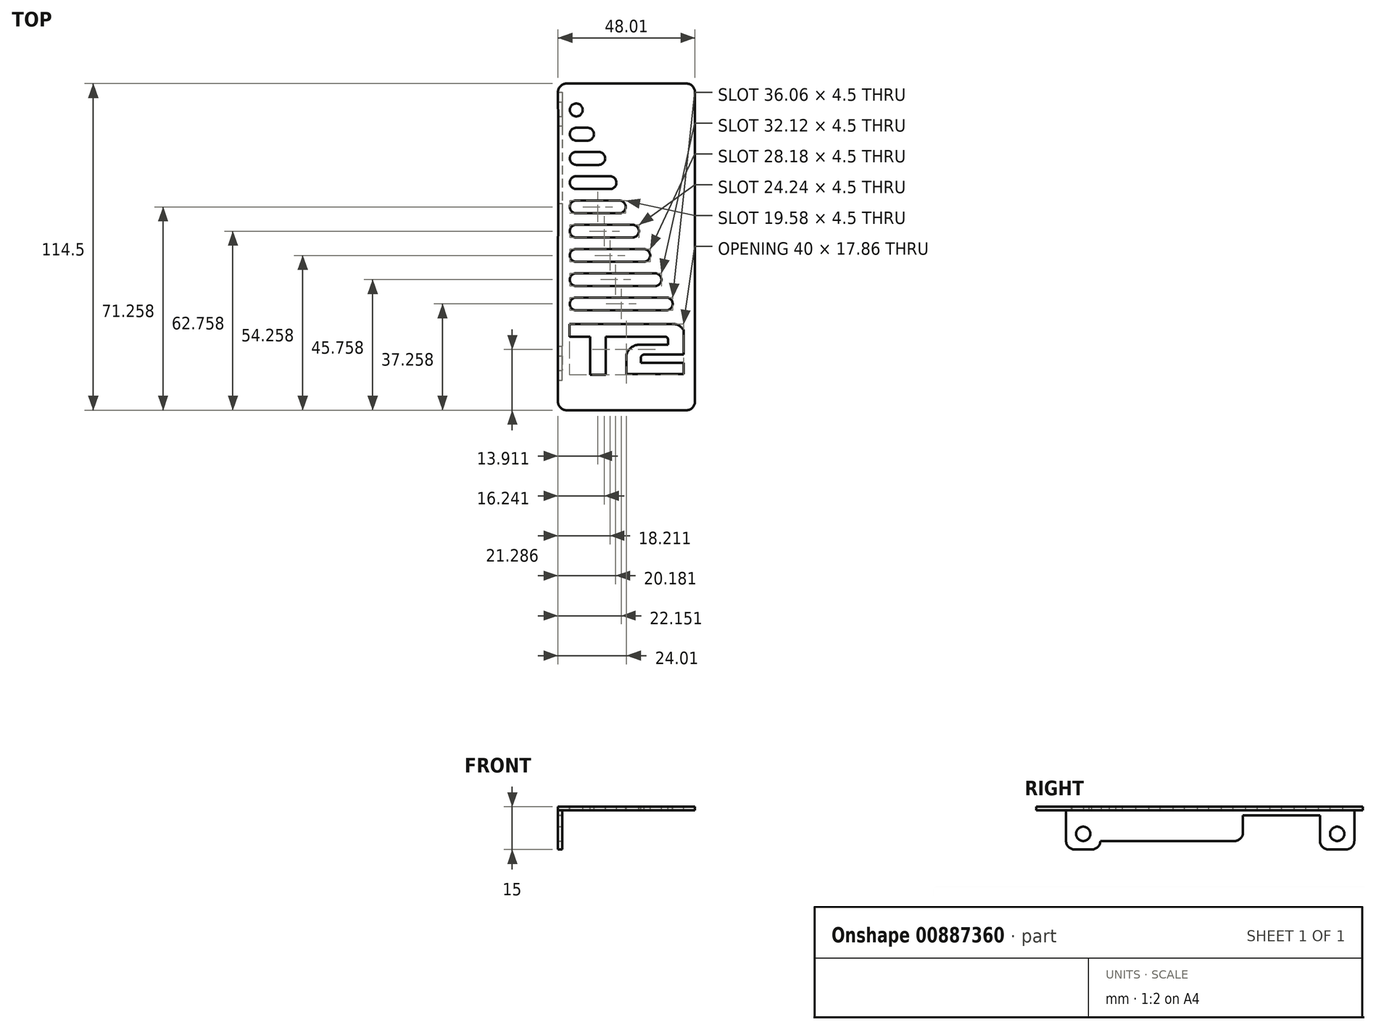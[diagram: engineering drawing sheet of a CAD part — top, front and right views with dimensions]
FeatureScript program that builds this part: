
annotation { "Feature Type Name" : "Feature", "Feature Type Description" : "" }
export const myFeature = defineFeature(function(context is Context, id is Id, definition is map)
    precondition{}
    {
        {
            var Q0;
            Q0=qCreatedBy(makeId("Top.planeOp"),FACE);
            var sketch = newSketch(context, id + "F0", { "sketchPlane" : qUnion([Q0])});
            skLineSegment(sketch, "E0.bottom", {"start": v(-24, 57.25) * mm, "end": v(24, 57.25) * mm});
            skLineSegment(sketch, "E0.right", {"start": v(24, 57.25) * mm, "end": v(24, -57.25) * mm});
            skPoint(sketch, "E0.middle", {"position": v(0, 0) * mm});
            skLineSegment(sketch, "E1", {"start": v(-20, -27.03) * mm, "end": v(-20, -31.53) * mm});
            skLineSegment(sketch, "E2", {"start": v(-12.75, -31.53) * mm, "end": v(-20, -31.53) * mm});
            skLineSegment(sketch, "E3", {"start": v(-12.75, -31.53) * mm, "end": v(-12.75, -44.9) * mm});
            skLineSegment(sketch, "E4", {"start": v(-12.75, -44.9) * mm, "end": v(-7.25, -44.9) * mm});
            skLineSegment(sketch, "E5", {"start": v(19.99, -40.62) * mm, "end": v(4.99, -40.62) * mm});
            skArc(sketch, "E6", {"start": v(4.33, -34.3) * mm, "mid": v(1.6, -35.34) * mm, "end": v(0, -37.8) * mm});
            skArc(sketch, "E7", {"start": v(6.16, -37.76) * mm, "mid": v(5.44, -38.04) * mm, "end": v(4.99, -38.66) * mm});
            skArc(sketch, "E8", {"start": v(20, -29.26) * mm, "mid": v(18.38, -27.56) * mm, "end": v(16.1, -27.03) * mm});
            skLineSegment(sketch, "E9", {"start": v(-20, -27.03) * mm, "end": v(16.1, -27.03) * mm});
            skLineSegment(sketch, "E10", {"start": v(4.99, -38.66) * mm, "end": v(4.99, -40.62) * mm});
            skLineSegment(sketch, "E11", {"start": v(6.16, -37.76) * mm, "end": v(20, -37.76) * mm});
            skLineSegment(sketch, "E12", {"start": v(20, -29.26) * mm, "end": v(20, -37.76) * mm});
            skLineSegment(sketch, "E13", {"start": v(4.33, -34.3) * mm, "end": v(14.5, -34.3) * mm});
            skLineSegment(sketch, "E14", {"start": v(-17.64, -22.24) * mm, "end": v(13.92, -22.24) * mm});
            skLineSegment(sketch, "E15", {"start": v(13.92, -17.74) * mm, "end": v(-17.64, -17.74) * mm});
            skArc(sketch, "E16", {"start": v(-17.64, -17.74) * mm, "mid": v(-19.89, -20) * mm, "end": v(-17.64, -22.24) * mm});
            skArc(sketch, "E17", {"start": v(13.92, -17.74) * mm, "mid": v(16.17, -20) * mm, "end": v(13.92, -22.24) * mm});
            skLineSegment(sketch, "E18", {"start": v(-17.64, -13.74) * mm, "end": v(9.98, -13.74) * mm});
            skLineSegment(sketch, "E19", {"start": v(9.98, -9.24) * mm, "end": v(-17.64, -9.24) * mm});
            skArc(sketch, "E20", {"start": v(-17.64, -9.24) * mm, "mid": v(-19.89, -11.5) * mm, "end": v(-17.64, -13.74) * mm});
            skArc(sketch, "E21", {"start": v(9.98, -9.24) * mm, "mid": v(12.23, -11.5) * mm, "end": v(9.98, -13.74) * mm});
            skLineSegment(sketch, "E22", {"start": v(-17.64, -5.24) * mm, "end": v(6.04, -5.24) * mm});
            skLineSegment(sketch, "E23", {"start": v(6.04, -0.74) * mm, "end": v(-17.64, -0.74) * mm});
            skArc(sketch, "E24", {"start": v(-17.64, -0.74) * mm, "mid": v(-19.89, -3) * mm, "end": v(-17.64, -5.24) * mm});
            skArc(sketch, "E25", {"start": v(6.04, -0.74) * mm, "mid": v(8.3, -3) * mm, "end": v(6.04, -5.24) * mm});
            skLineSegment(sketch, "E26", {"start": v(-17.64, 3.26) * mm, "end": v(2.1, 3.26) * mm});
            skLineSegment(sketch, "E27", {"start": v(2.1, 7.76) * mm, "end": v(-17.64, 7.76) * mm});
            skArc(sketch, "E28", {"start": v(-17.64, 7.76) * mm, "mid": v(-19.89, 5.5) * mm, "end": v(-17.64, 3.26) * mm});
            skArc(sketch, "E29", {"start": v(2.1, 7.76) * mm, "mid": v(4.35, 5.5) * mm, "end": v(2.1, 3.26) * mm});
            skLineSegment(sketch, "E30", {"start": v(-17.64, 11.76) * mm, "end": v(-2.56, 11.76) * mm});
            skLineSegment(sketch, "E31", {"start": v(-2.56, 16.26) * mm, "end": v(-17.64, 16.26) * mm});
            skArc(sketch, "E32", {"start": v(-17.64, 16.26) * mm, "mid": v(-19.89, 14) * mm, "end": v(-17.64, 11.76) * mm});
            skArc(sketch, "E33", {"start": v(-2.56, 16.26) * mm, "mid": v(-0.3, 14) * mm, "end": v(-2.56, 11.76) * mm});
            skLineSegment(sketch, "E34", {"start": v(-17.64, 20.26) * mm, "end": v(-5.78, 20.26) * mm});
            skLineSegment(sketch, "E35", {"start": v(-5.78, 24.76) * mm, "end": v(-17.64, 24.76) * mm});
            skArc(sketch, "E36", {"start": v(-17.64, 24.76) * mm, "mid": v(-19.89, 22.5) * mm, "end": v(-17.64, 20.26) * mm});
            skArc(sketch, "E37", {"start": v(-5.78, 24.76) * mm, "mid": v(-3.53, 22.5) * mm, "end": v(-5.78, 20.26) * mm});
            skLineSegment(sketch, "E38", {"start": v(-17.64, 28.76) * mm, "end": v(-9.72, 28.76) * mm});
            skLineSegment(sketch, "E39", {"start": v(-9.72, 33.26) * mm, "end": v(-17.64, 33.26) * mm});
            skArc(sketch, "E40", {"start": v(-17.64, 33.26) * mm, "mid": v(-19.89, 31) * mm, "end": v(-17.64, 28.76) * mm});
            skArc(sketch, "E41", {"start": v(-9.72, 33.26) * mm, "mid": v(-7.47, 31) * mm, "end": v(-9.72, 28.76) * mm});
            skLineSegment(sketch, "E42", {"start": v(-17.64, 37.26) * mm, "end": v(-13.66, 37.26) * mm});
            skLineSegment(sketch, "E43", {"start": v(-13.66, 41.76) * mm, "end": v(-17.64, 41.76) * mm});
            skArc(sketch, "E44", {"start": v(-17.64, 41.76) * mm, "mid": v(-19.89, 39.5) * mm, "end": v(-17.64, 37.26) * mm});
            skArc(sketch, "E45", {"start": v(-13.66, 41.76) * mm, "mid": v(-11.4, 39.5) * mm, "end": v(-13.66, 37.26) * mm});
            skLineSegment(sketch, "E46", {"start": v(-17.64, 45.76) * mm, "end": v(-17.6, 45.76) * mm});
            skLineSegment(sketch, "E47", {"start": v(-17.6, 50.26) * mm, "end": v(-17.64, 50.26) * mm});
            skArc(sketch, "E48", {"start": v(-17.64, 50.26) * mm, "mid": v(-19.89, 48) * mm, "end": v(-17.64, 45.76) * mm});
            skArc(sketch, "E49", {"start": v(-17.6, 50.26) * mm, "mid": v(-15.35, 48) * mm, "end": v(-17.6, 45.76) * mm});
            skLineSegment(sketch, "E50", {"start": v(-7.25, -44.9) * mm, "end": v(-7.25, -31.53) * mm});
            skLineSegment(sketch, "E51", {"start": v(19.99, -40.62) * mm, "end": v(20, -44.62) * mm});
            skLineSegment(sketch, "E52", {"start": v(0, -37.8) * mm, "end": v(0, -44.62) * mm});
            skLineSegment(sketch, "E53", {"start": v(0, -44.62) * mm, "end": v(20, -44.62) * mm});
            skArc(sketch, "E54", {"start": v(14.5, -32.31) * mm, "mid": v(14.27, -31.76) * mm, "end": v(13.72, -31.53) * mm});
            skLineSegment(sketch, "E55", {"start": v(14.5, -32.31) * mm, "end": v(14.5, -34.3) * mm});
            skLineSegment(sketch, "E56", {"start": v(-7.25, -31.53) * mm, "end": v(13.72, -31.53) * mm});
            skLineSegment(sketch, "E57", {"start": v(-24, -57.25) * mm, "end": v(24, -57.25) * mm});
            skLineSegment(sketch, "E58", {"start": v(-24, 57.25) * mm, "end": v(-24, 54.25) * mm});
            skLineSegment(sketch, "E59", {"start": v(-24, 54.25) * mm, "end": v(-22.5, 54.25) * mm});
            skLineSegment(sketch, "E60", {"start": v(-22.5, 54.25) * mm, "end": v(-22.5, 42.25) * mm});
            skLineSegment(sketch, "E61", {"start": v(-22.5, 42.25) * mm, "end": v(-23.94, 42.25) * mm});
            skPoint(sketch, "E62", {"position": v(-24, -46.75) * mm});
            skLineSegment(sketch, "E63", {"start": v(-24, -46.75) * mm, "end": v(-22.5, -46.75) * mm});
            skLineSegment(sketch, "E64", {"start": v(-22.5, -46.75) * mm, "end": v(-22.5, -34.75) * mm});
            skLineSegment(sketch, "E65", {"start": v(-24, -46.75) * mm, "end": v(-24, -34.75) * mm});
            skLineSegment(sketch, "E66", {"start": v(-24, -34.75) * mm, "end": v(-22.5, -34.75) * mm});
            skLineSegment(sketch, "E67", {"start": v(-24, -57.25) * mm, "end": v(-24, -46.75) * mm});
            skLineSegment(sketch, "E68", {"start": v(-24, 54.25) * mm, "end": v(-23.94, 42.25) * mm});
            skLineSegment(sketch, "E69", {"start": v(-24, -34.75) * mm, "end": v(-23.96, 15.25) * mm});
            skLineSegment(sketch, "E70", {"start": v(-23.96, 15.25) * mm, "end": v(-22.5, 15.25) * mm});
            skLineSegment(sketch, "E71", {"start": v(-22.5, 15.25) * mm, "end": v(-22.5, -34.75) * mm});
            skLineSegment(sketch, "E72", {"start": v(-23.94, 42.25) * mm, "end": v(-23.96, 15.25) * mm});
            skLineSegment(sketch, "E73", {"start": v(-22.5, 42.25) * mm, "end": v(-22.5, 15.25) * mm});
            skSolve(sketch);
        }
        {
            var Q0;
            Q0=makeQuery(id+"F0.imprint","IMPRINT",FACE,{"disambiguationData":[TD([[makeQuery(id+"F0.imprint","IMPRINT",EDGE,{"derivedFrom":sQuery(id+"F0.wireOp",EDGE,"E0.bottom")}),-1.0]])]});
            var Q1;
            Q1 = qSketchRegion(id + "F3", true);
            extrude(context, id + "F1", {"entities" : qUnion([Q0, Q1]), "oppositeDirection" : true, "depth" : 1.2 * mm, "offsetDistance" : 25 * mm});
        }
        {
            var Q0;
            Q0=makeQuery(id+"F0.imprint","IMPRINT",FACE,{"disambiguationData":[TD([[makeQuery(id+"F0.imprint","IMPRINT",EDGE,{"derivedFrom":sQuery(id+"F0.wireOp",EDGE,"E59")}),-1.0]])]});
            var Q1;
            Q1=makeQuery(id+"F0.imprint","IMPRINT",FACE,{"disambiguationData":[TD([[makeQuery(id+"F0.imprint","IMPRINT",EDGE,{"derivedFrom":sQuery(id+"F0.wireOp",EDGE,"E63")}),1.0]])]});
            extrude(context, id + "F2", {"entities" : qUnion([Q0, Q1]), "operationType" : NewBodyOperationType.ADD, "oppositeDirection" : true, "depth" : 15 * mm, "offsetDistance" : 25 * mm});
        }
        {
            var Q0;
            Q0=qCreatedBy(makeId("Right.planeOp"),FACE);
            var sketch = newSketch(context, id + "F3", { "sketchPlane" : qUnion([Q0])});
            skPoint(sketch, "E74", {"position": v(-40.75, -9.5) * mm});
            skPoint(sketch, "E75", {"position": v(48.25, -9.5) * mm});
            skSolve(sketch);
        }
        {
            var Q0;
            Q0=sQuery(id+"F3.wireOp",VERTEX,"E74");
            var Q1;
            Q1=sQuery(id+"F3.wireOp",VERTEX,"E75");
            var Q2;
            Q2=makeQuery(id+"F1.opExtrude","SWEPT_BODY",BODY,{"disambiguationData":[OSD([sQuery(id+"F0.wireOp",EDGE,"E0.bottom"),sQuery(id+"F0.wireOp",EDGE,"E0.top"),sQuery(id+"F0.wireOp",EDGE,"E0.right"),sQuery(id+"F0.wireOp",EDGE,"E1"),sQuery(id+"F0.wireOp",EDGE,"E2"),sQuery(id+"F0.wireOp",EDGE,"E3"),sQuery(id+"F0.wireOp",EDGE,"E4"),sQuery(id+"F0.wireOp",EDGE,"0LANiQkd-xG1w-0jAY-0H3d-zRR3qAL3rn1X"),sQuery(id+"F0.wireOp",EDGE,"E5"),sQuery(id+"F0.wireOp",EDGE,"E6"),sQuery(id+"F0.wireOp",EDGE,"E7"),sQuery(id+"F0.wireOp",EDGE,"E8"),sQuery(id+"F0.wireOp",EDGE,"E9"),sQuery(id+"F0.wireOp",EDGE,"E10"),sQuery(id+"F0.wireOp",EDGE,"E11"),sQuery(id+"F0.wireOp",EDGE,"E12"),sQuery(id+"F0.wireOp",EDGE,"E13"),sQuery(id+"F0.wireOp",EDGE,"H3LriEdK-IGWu-km3t-O8Rp-QvWeqxySHV8o"),sQuery(id+"F0.wireOp",EDGE,"EcIqTxym-PrgU-ehmv-7TEX-s5XfxjkhuH4a"),sQuery(id+"F0.wireOp",EDGE,"6be5b86a-f134-4340-a0f3-9762bb9dc0c5"),sQuery(id+"F0.wireOp",EDGE,"d7688d6a-630d-4f20-921e-fb5fbf414a30"),sQuery(id+"F0.wireOp",EDGE,"E14"),sQuery(id+"F0.wireOp",EDGE,"E15"),sQuery(id+"F0.wireOp",EDGE,"E16"),sQuery(id+"F0.wireOp",EDGE,"E17"),sQuery(id+"F0.wireOp",EDGE,"E18"),sQuery(id+"F0.wireOp",EDGE,"E19"),sQuery(id+"F0.wireOp",EDGE,"E20"),sQuery(id+"F0.wireOp",EDGE,"E21"),sQuery(id+"F0.wireOp",EDGE,"E22"),sQuery(id+"F0.wireOp",EDGE,"E23"),sQuery(id+"F0.wireOp",EDGE,"E24"),sQuery(id+"F0.wireOp",EDGE,"E25"),sQuery(id+"F0.wireOp",EDGE,"E26"),sQuery(id+"F0.wireOp",EDGE,"E27"),sQuery(id+"F0.wireOp",EDGE,"E28"),sQuery(id+"F0.wireOp",EDGE,"E29"),sQuery(id+"F0.wireOp",EDGE,"E30"),sQuery(id+"F0.wireOp",EDGE,"E31"),sQuery(id+"F0.wireOp",EDGE,"E32"),sQuery(id+"F0.wireOp",EDGE,"E33"),sQuery(id+"F0.wireOp",EDGE,"E34"),sQuery(id+"F0.wireOp",EDGE,"E35"),sQuery(id+"F0.wireOp",EDGE,"E36"),sQuery(id+"F0.wireOp",EDGE,"E37"),sQuery(id+"F0.wireOp",EDGE,"E38"),sQuery(id+"F0.wireOp",EDGE,"E39"),sQuery(id+"F0.wireOp",EDGE,"E40"),sQuery(id+"F0.wireOp",EDGE,"E41"),sQuery(id+"F0.wireOp",EDGE,"E42"),sQuery(id+"F0.wireOp",EDGE,"E43"),sQuery(id+"F0.wireOp",EDGE,"E44"),sQuery(id+"F0.wireOp",EDGE,"E45"),sQuery(id+"F0.wireOp",EDGE,"E46"),sQuery(id+"F0.wireOp",EDGE,"E47"),sQuery(id+"F0.wireOp",EDGE,"E48"),sQuery(id+"F0.wireOp",EDGE,"E49"),sQuery(id+"F0.wireOp",EDGE,"E50"),sQuery(id+"F0.wireOp",EDGE,"E51"),sQuery(id+"F0.wireOp",EDGE,"E52"),sQuery(id+"F0.wireOp",EDGE,"E53"),sQuery(id+"F0.wireOp",EDGE,"E54"),sQuery(id+"F0.wireOp",EDGE,"E55"),sQuery(id+"F0.wireOp",EDGE,"E56")])]});
            hole(context, id + "F4", {"style" : HoleStyle.SIMPLE, "endStyle" : HoleEndStyle.THROUGH, "holeDiameter" : 5 * mm, "majorDiameter" : 5 * mm, "isTappedThrough" : true, "tappedDepth" : 12 * mm, "tapClearance" : 3, "locations" : qUnion([Q0, Q1]), "scope" : qUnion([Q2])});
        }
        {
            var Q0;
            Q0=makeQuery(id+"F2.opExtrude","CAP_EDGE",EDGE,{"disambiguationData":[OSD([sQuery(id+"F0.wireOp",EDGE,"HBLAxpmw-sJ8A-g88T-pWDY-p4oM08mXjc2A")])],"isStart":false});
            var Q1;
            Q1=makeQuery(id+"F2.opExtrude","CAP_EDGE",EDGE,{"disambiguationData":[OSD([sQuery(id+"F0.wireOp",EDGE,"E61")])],"isStart":false});
            var Q2;
            Q2=makeQuery(id+"F2.opExtrude","CAP_EDGE",EDGE,{"disambiguationData":[OSD([sQuery(id+"F0.wireOp",EDGE,"E59")])],"isStart":false});
            var Q3;
            Q3=makeQuery(id+"F2.opExtrude","CAP_EDGE",EDGE,{"disambiguationData":[OSD([sQuery(id+"F0.wireOp",EDGE,"z9CvzlAU-oE5h-fNBz-gN4p-R0uBhrxic2hj")])],"isStart":false});
            var Q4;
            Q4=makeQuery(id+"F2.opExtrude","CAP_EDGE",EDGE,{"disambiguationData":[OSD([sQuery(id+"F0.wireOp",EDGE,"E66")])],"isStart":false});
            var Q5;
            Q5=makeQuery(id+"F2.opExtrude","CAP_EDGE",EDGE,{"disambiguationData":[OSD([sQuery(id+"F0.wireOp",EDGE,"E63")])],"isStart":false});
            fillet(context, id + "F5", {"entities" : qUnion([Q0, Q1, Q2, Q3, Q4, Q5]), "radius" : 3 * mm, "tangentPropagation" : true, "allowEdgeOverflow" : false});
        }
        {
            var Q0;
            Q0=makeQuery(id+"F0.imprint","IMPRINT",FACE,{"disambiguationData":[TD([[makeQuery(id+"F0.imprint","IMPRINT",EDGE,{"derivedFrom":sQuery(id+"F0.wireOp",EDGE,"E61")}),1.0]])]});
            extrude(context, id + "F6", {"entities" : qUnion([Q0]), "operationType" : NewBodyOperationType.ADD, "oppositeDirection" : true, "depth" : 3 * mm, "offsetDistance" : 25 * mm});
        }
        {
            var Q0;
            Q0=makeQuery(id+"F0.imprint","IMPRINT",FACE,{"disambiguationData":[TD([[makeQuery(id+"F0.imprint","IMPRINT",EDGE,{"derivedFrom":sQuery(id+"F0.wireOp",EDGE,"E66")}),1.0]])]});
            extrude(context, id + "F7", {"entities" : qUnion([Q0]), "operationType" : NewBodyOperationType.ADD, "oppositeDirection" : true, "depth" : 12 * mm, "offsetDistance" : 25 * mm});
        }
        {
            var Q0;
            Q0=makeQuery(id+"F7.opExtrude","CAP_EDGE",EDGE,{"disambiguationData":[OSD([sQuery(id+"F0.wireOp",EDGE,"E70")])],"isStart":false});
            var Q1;
            Q1=makeQuery(id+"F1.opExtrude","SWEPT_EDGE",EDGE,{"disambiguationData":[OSD([sQuery(id+"F0.wireOp",EDGE,"E0.bottom"),sQuery(id+"F0.wireOp",EDGE,"E0.right")])]});
            var Q2;
            Q2=makeQuery(id+"F1.opExtrude","SWEPT_EDGE",EDGE,{"disambiguationData":[OSD([sQuery(id+"F0.wireOp",EDGE,"E0.bottom"),sQuery(id+"F0.wireOp",EDGE,"E58")])]});
            var Q3;
            Q3=makeQuery(id+"F1.opExtrude","SWEPT_EDGE",EDGE,{"disambiguationData":[OSD([sQuery(id+"F0.wireOp",EDGE,"E57"),sQuery(id+"F0.wireOp",EDGE,"E67")])]});
            var Q4;
            Q4=makeQuery(id+"F1.opExtrude","SWEPT_EDGE",EDGE,{"disambiguationData":[OSD([sQuery(id+"F0.wireOp",EDGE,"E0.right"),sQuery(id+"F0.wireOp",EDGE,"E57")])]});
            fillet(context, id + "F8", {"entities" : qUnion([Q0, Q1, Q2, Q3, Q4]), "radius" : 3 * mm, "tangentPropagation" : true, "allowEdgeOverflow" : false});
        }
    });
